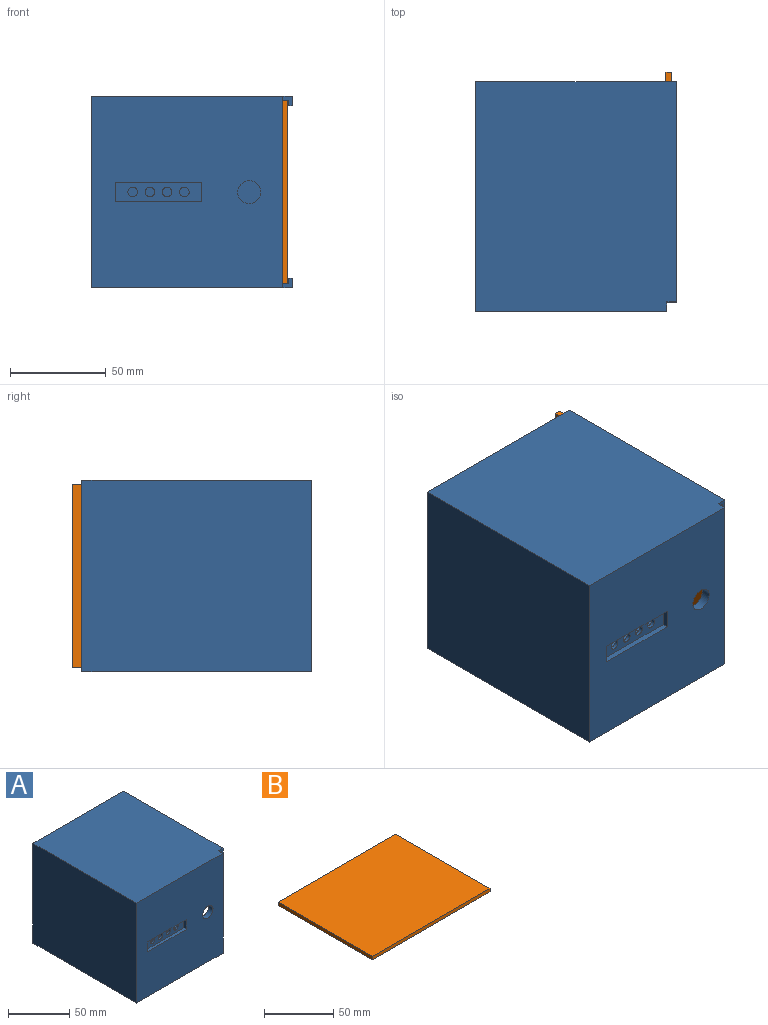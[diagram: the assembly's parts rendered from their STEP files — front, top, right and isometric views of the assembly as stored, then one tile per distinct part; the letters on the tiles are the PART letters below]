
ASSEMBLY  parts=2 mates=1
PART A: 45 faces, bbox 105x120x100 mm
  f0: plane 110x95mm, normal (0,0,-1), area 10450mm2, adj f3,f19,f20,f23
  f1: plane 115x2mm, normal (0,0,1), area 230mm2, adj f2,f8,f38,f41
  f2: plane 5x5mm, normal (0,-1,0), area 16mm2, adj f1,f3,f7,f38,f41,f42
  f3: plane 120x100mm, normal (1,0,0), area 1640mm2, adj f0,f2,f4,f5,f7,f8,f19,f20
  f4: plane 100x100mm, normal (0,-1,0), area 9436.9mm2, adj f3,f5,f6,f7,f9,f10,f11,f12
  f5: plane 120x105mm, normal (0,0,1), area 12575mm2, adj f3,f4,f6,f8,f39,f40
  f6: plane 120x100mm, normal (-1,0,0), area 12000mm2, adj f4,f5,f7,f8
  f7: plane 120x105mm, normal (0,0,-1), area 12575mm2, adj f2,f3,f4,f6,f8,f38
  f8: plane 105x100mm, normal (0,1,0), area 10032mm2, adj f1,f3,f5,f6,f7,f21,f38,f40
  f9: plane 10x3mm, normal (-1,0,0), area 30mm2, adj f4,f10,f12,f13
  f10: plane 45x3mm, normal (0,0,-1), area 135mm2, adj f4,f9,f11,f13
  f11: plane 10x3mm, normal (1,0,0), area 30mm2, adj f4,f10,f12,f13
  f12: plane 45x3mm, normal (0,0,1), area 135mm2, adj f4,f9,f11,f13
  f13: plane 45x10mm, normal (0,-1,0), area 371.5mm2, adj f9,f10,f11,f12,f15,f16,f17,f18
  f14: cylinder r=6mm len=12mm, axis (0,-1,0), area 188.5mm2, adj f4,f19
  f15: cylinder r=2.5mm len=5mm, axis (0,-1,0), area 31.4mm2, adj f13,f19
  f16: cylinder r=2.5mm len=5mm, axis (0,-1,0), area 31.4mm2, adj f13,f19
  f17: cylinder r=2.5mm len=5mm, axis (0,-1,0), area 31.4mm2, adj f13,f19
  f18: cylinder r=2.5mm len=5mm, axis (0,-1,0), area 31.4mm2, adj f13,f19
  f19: plane 95x90mm, normal (0,1,0), area 7959.4mm2, adj f0,f3,f14,f15,f16,f17,f18,f22
  f20: plane 95x90mm, normal (0,-1,0), area 8250mm2, adj f0,f3,f22,f23,f28,f29,f30,f31
  f21: plane 115x2mm, normal (0,0,-1), area 230mm2, adj f8,f39,f40,f43
  f22: plane 110x95mm, normal (0,0,1), area 10450mm2, adj f3,f19,f20,f23
  f23: plane 110x90mm, normal (1,0,0), area 9650mm2, adj f0,f19,f20,f22,f24,f25,f27
  f24: plane 60x50mm, normal (0,0,-1), area 3000mm2, adj f19,f23,f26,f27
  f25: plane 60x50mm, normal (0,0,1), area 3000mm2, adj f19,f23,f26,f27
  f26: plane 50x5mm, normal (1,0,0), area 250mm2, adj f19,f24,f25,f27
  f27: plane 60x5mm, normal (0,1,0), area 300mm2, adj f23,f24,f25,f26
  f28: plane 45x5mm, normal (1,0,0), area 225mm2, adj f20,f29,f31,f32
  f29: plane 60x45mm, normal (0,0,1), area 2700mm2, adj f20,f28,f30,f32
  f30: plane 45x5mm, normal (-1,0,0), area 225mm2, adj f20,f29,f31,f32
  f31: plane 60x45mm, normal (0,0,-1), area 2700mm2, adj f20,f28,f30,f32
  f32: plane 60x5mm, normal (0,-1,0), area 300mm2, adj f28,f29,f30,f31
  f33: plane 33x15mm, normal (0,0,1), area 495mm2, adj f19,f34,f36,f37
  f34: plane 15x3mm, normal (1,0,0), area 45mm2, adj f19,f33,f35,f37
  f35: plane 33x15mm, normal (0,0,-1), area 495mm2, adj f19,f34,f36,f37
  f36: plane 15x3mm, normal (-1,0,0), area 45mm2, adj f19,f33,f35,f37
  f37: plane 33x3mm, normal (0,1,0), area 99mm2, adj f33,f34,f35,f36
  f38: plane 115x5mm, normal (1,0,0), area 575mm2, adj f1,f2,f7,f8
  f39: plane 5x5mm, normal (0,-1,0), area 16mm2, adj f3,f5,f21,f40,f43,f44
  f40: plane 115x5mm, normal (1,0,0), area 575mm2, adj f5,f8,f21,f39
  f41: plane 115x3mm, normal (-1,0,0), area 345mm2, adj f1,f2,f8,f42
  f42: plane 115x3mm, normal (0,0,1), area 345mm2, adj f2,f3,f8,f41
  f43: plane 115x3mm, normal (-1,0,0), area 345mm2, adj f8,f21,f39,f44
  f44: plane 115x3mm, normal (0,0,-1), area 345mm2, adj f3,f8,f39,f43
PART B: 6 faces, bbox 120x96x3 mm
  f0: plane 96x3mm, normal (1,0,0), area 288mm2, adj f1,f3,f4,f5
  f1: plane 120x3mm, normal (0,1,0), area 360mm2, adj f0,f2,f4,f5
  f2: plane 96x3mm, normal (-1,0,0), area 288mm2, adj f1,f3,f4,f5
  f3: plane 120x3mm, normal (0,-1,0), area 360mm2, adj f0,f2,f4,f5
  f4: plane 120x96mm, normal (0,0,1), area 11520mm2, adj f0,f1,f2,f3
  f5: plane 120x96mm, normal (0,0,-1), area 11520mm2, adj f0,f1,f2,f3
PLACE A at identity fixed
PLACE B rot(axis=(-0.58,0.58,-0.58),120deg) t=(49.5,5,0)mm
MATE slider B.f0 <-> A.f19  axis (0,-1,0) through (51,-55,0)mm
